# Revit family: LTC-3RDW-S
name_source: partatom
category: Lighting Fixtures
revit_build: Autodesk Revit 2014 (Build: 20130308_1515(x64)
units: mm (PartAtom-declared; Revit-internal decimal feet)

## types (1)
- LTC-3RW-S
    Apparent Load = 52 VA
    Ceiling Cutout = 6 1/2"
    Color Filter = 16777215
    Connector Description = Lighting Connector
    Cutout Radius = 3"
    Default Elevation = 48"
    Description = LITEISTRY™ 3 Round Cylinder Downlight/Wall Wash
    Dimming Lamp Color Temperature Shift = <None>
    Emit Shape Visible in Rendering = Yes
    Emit from Circle Diameter = 3"
    Frequency = 60 Hz
    Glass = Hubbell - White Glass
    Is 120V = Yes
    Is 277V = No
    Lamp = LED's
    Load Classification = Lighting
    Manufacturer = Prescolite
    Model = LTC-3RD
    Photometric Notes = More IES files download on Photometric Web Link
    Photometric Web File = LTC-3RD-P-20L35K8MD-DM1-S-BL.ies
    Photometric Web Link = https://www.hubbell.com
    Product Documentation Link = https://hubbellcdn.com
    Product Material = Paint - Hubbell - Carbon Black
    Product Page URL = https://www.hubbell.com
    Reflector Finish = Paint - Hubbell - Carbon Black
    Tilt Angle = -90.00°
    URL = https://www.hubbell.com
    Voltage = 120 V

## geometry (parser evidence)
native form markers: Blend x4, Sweep x1
no freeform markers — native parametric forms only
